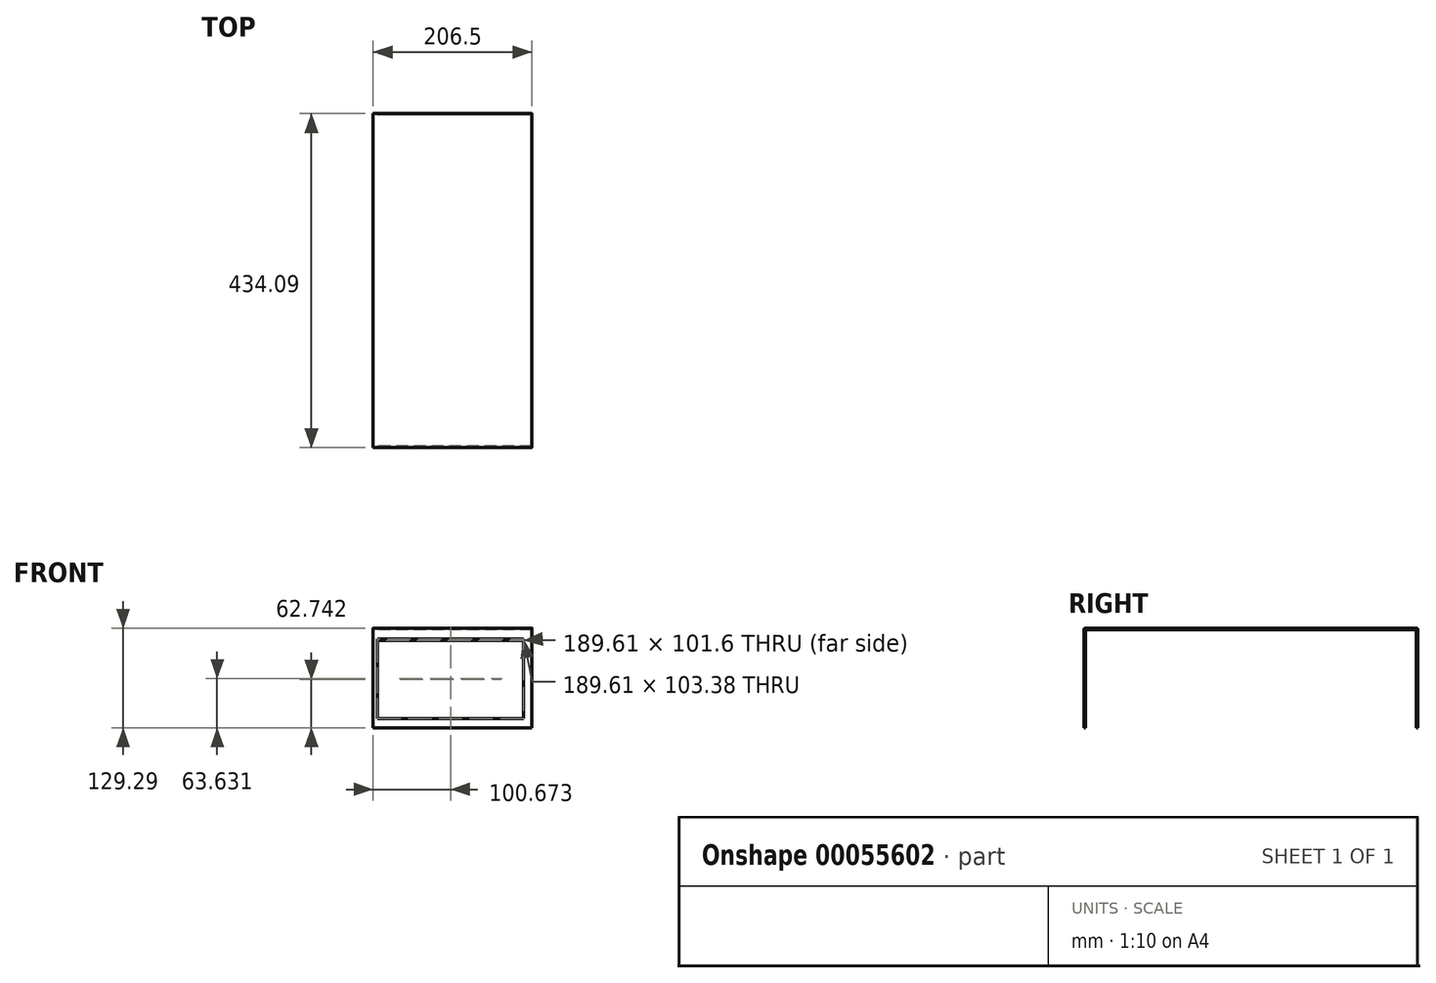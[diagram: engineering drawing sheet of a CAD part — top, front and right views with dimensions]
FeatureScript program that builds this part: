
annotation { "Feature Type Name" : "Feature", "Feature Type Description" : "" }
export const myFeature = defineFeature(function(context is Context, id is Id, definition is map)
    precondition{}
    {
        {
            var Q0;
            Q0=qCreatedBy(makeId("Right.planeOp"),FACE);
            var sketch = newSketch(context, id + "F0", { "sketchPlane" : qUnion([Q0])});
            skLineSegment(sketch, "E0", {"start": v(1.78, 0) * mm, "end": v(432.3, 0) * mm});
            skLineSegment(sketch, "E1", {"start": v(434.09, -1.78) * mm, "end": v(434.09, -129.29) * mm});
            skLineSegment(sketch, "E2", {"start": v(0, -1.78) * mm, "end": v(0, -129.29) * mm});
            skLineSegment(sketch, "E3", {"start": v(0, -129.29) * mm, "end": v(2.03, -129.29) * mm});
            skLineSegment(sketch, "E4", {"start": v(2.03, -129.29) * mm, "end": v(2.03, -2.03) * mm});
            skLineSegment(sketch, "E5", {"start": v(2.03, -2.03) * mm, "end": v(432.05, -2.03) * mm});
            skLineSegment(sketch, "E6", {"start": v(432.05, -2.03) * mm, "end": v(432.05, -129.29) * mm});
            skLineSegment(sketch, "E7", {"start": v(432.05, -129.29) * mm, "end": v(434.09, -129.29) * mm});
            skPoint(sketch, "E8.visualSharp", {"position": v(0, 0) * mm});
            skArc(sketch, "E8.filletArc", {"start": v(1.78, 0) * mm, "mid": v(0.52, -0.52) * mm, "end": v(0, -1.78) * mm});
            skPoint(sketch, "E9.visualSharp", {"position": v(434.09, 0) * mm});
            skArc(sketch, "E9.filletArc", {"start": v(434.09, -1.78) * mm, "mid": v(433.57, -0.52) * mm, "end": v(432.3, 0) * mm});
            skSolve(sketch);
        }
        {
            var Q0;
            Q0=makeQuery(id+"F0.imprint","IMPRINT",FACE,{"disambiguationData":[TD([[makeQuery(id+"F0.imprint","IMPRINT",EDGE,{"derivedFrom":sQuery(id+"F0.wireOp",EDGE,"E0")}),-1.0]])]});
            extrude(context, id + "F1", {"entities" : qUnion([Q0]), "depth" : 206.5 * mm});
        }
        {
            var Q0;
            Q0=makeQuery(id+"F1.opExtrude","SWEPT_FACE",FACE,{"disambiguationData":[OSD([sQuery(id+"F0.wireOp",EDGE,"E2")])]});
            var sketch = newSketch(context, id + "F2", { "sketchPlane" : qUnion([Q0])});
            skLineSegment(sketch, "E10.bottom", {"start": v(5.87, -13.97) * mm, "end": v(195.48, -13.97) * mm});
            skLineSegment(sketch, "E10.top", {"start": v(5.87, -117.35) * mm, "end": v(195.48, -117.35) * mm});
            skLineSegment(sketch, "E10.left", {"start": v(5.87, -13.97) * mm, "end": v(5.87, -117.35) * mm});
            skLineSegment(sketch, "E10.right", {"start": v(195.48, -13.97) * mm, "end": v(195.48, -117.35) * mm});
            skSolve(sketch);
        }
        {
            var Q0;
            Q0=makeQuery(id+"F2.imprint","IMPRINT",FACE,{"disambiguationData":[TD([[makeQuery(id+"F2.imprint","IMPRINT",EDGE,{"derivedFrom":sQuery(id+"F2.wireOp",EDGE,"E10.bottom")}),-1.0]])]});
            extrude(context, id + "F3", {"entities" : qUnion([Q0]), "operationType" : NewBodyOperationType.REMOVE, "oppositeDirection" : true, "depth" : 25.4 * mm});
        }
        {
            var Q0;
            Q0=makeQuery(id+"F1.opExtrude","SWEPT_FACE",FACE,{"disambiguationData":[OSD([sQuery(id+"F0.wireOp",EDGE,"E1")])]});
            var sketch = newSketch(context, id + "F4", { "sketchPlane" : qUnion([Q0])});
            skLineSegment(sketch, "E11.bottom", {"start": v(-195.48, -15.75) * mm, "end": v(-5.87, -15.75) * mm});
            skLineSegment(sketch, "E11.top", {"start": v(-195.48, -117.35) * mm, "end": v(-5.87, -117.35) * mm});
            skLineSegment(sketch, "E11.left", {"start": v(-195.48, -15.75) * mm, "end": v(-195.48, -117.35) * mm});
            skLineSegment(sketch, "E11.right", {"start": v(-5.87, -15.75) * mm, "end": v(-5.87, -117.35) * mm});
            skSolve(sketch);
        }
        {
            var Q0;
            Q0=makeQuery(id+"F4.imprint","IMPRINT",FACE,{"disambiguationData":[TD([[makeQuery(id+"F4.imprint","IMPRINT",EDGE,{"derivedFrom":sQuery(id+"F4.wireOp",EDGE,"E11.bottom")}),-1.0]])]});
            extrude(context, id + "F5", {"entities" : qUnion([Q0]), "operationType" : NewBodyOperationType.REMOVE, "oppositeDirection" : true, "depth" : 25.4 * mm});
        }
    });
